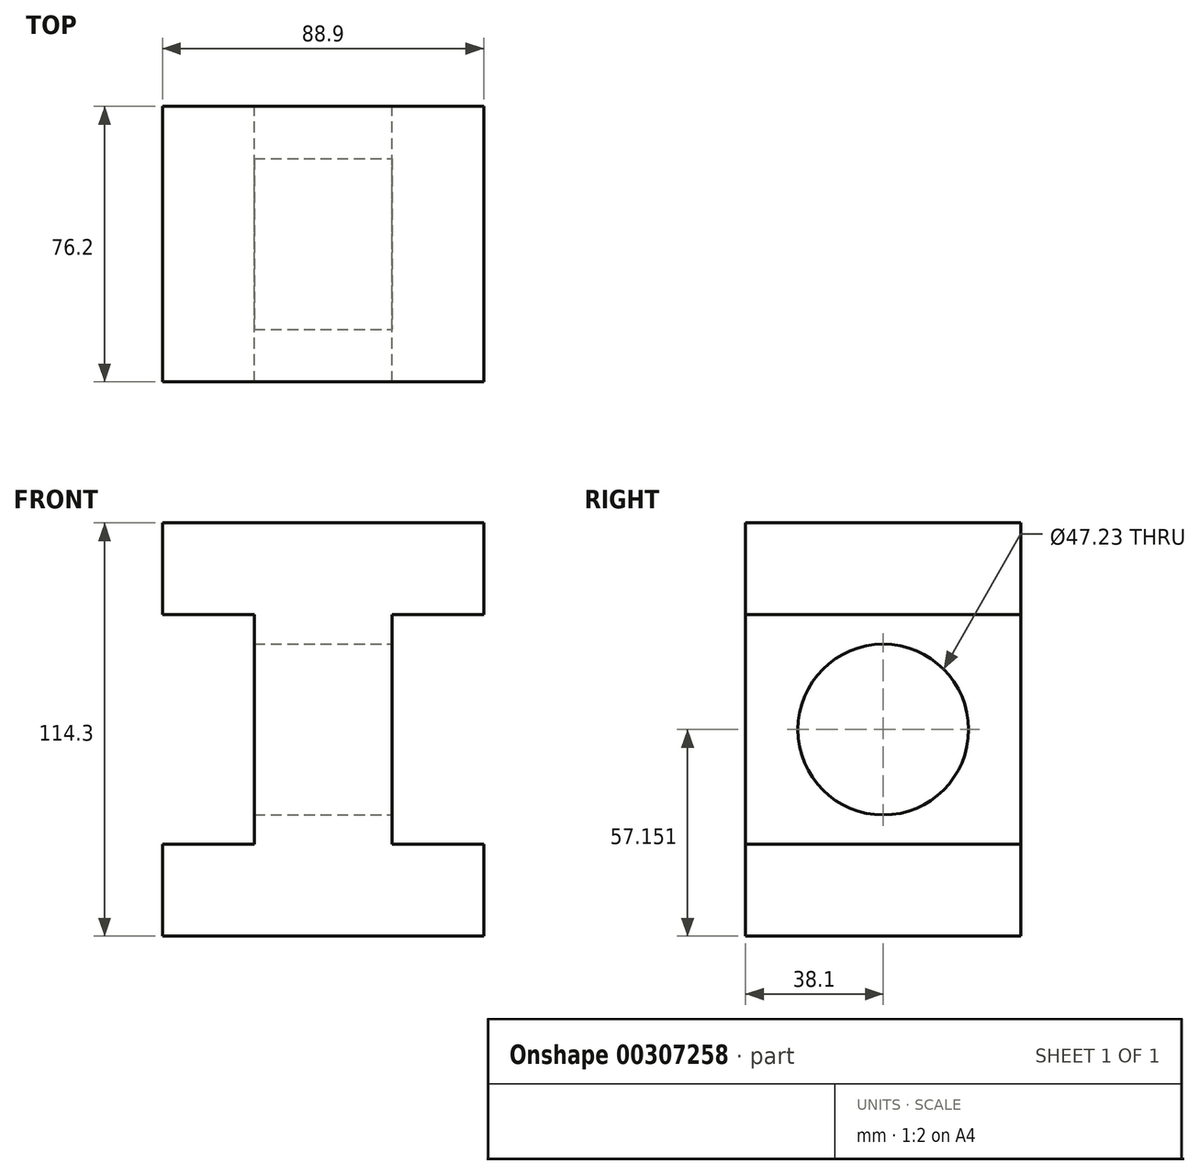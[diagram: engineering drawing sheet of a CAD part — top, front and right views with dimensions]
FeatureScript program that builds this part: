
annotation { "Feature Type Name" : "Feature", "Feature Type Description" : "" }
export const myFeature = defineFeature(function(context is Context, id is Id, definition is map)
    precondition{}
    {
        {
            var Q0;
            Q0=qCreatedBy(makeId("Front.planeOp"),FACE);
            var sketch = newSketch(context, id + "F0", { "sketchPlane" : qUnion([Q0])});
            skLineSegment(sketch, "E0", {"start": v(-48.35, -53.95) * mm, "end": v(40.55, -53.95) * mm});
            skLineSegment(sketch, "E1", {"start": v(40.55, -53.95) * mm, "end": v(40.55, -28.55) * mm});
            skLineSegment(sketch, "E2", {"start": v(40.55, -28.55) * mm, "end": v(15.15, -28.55) * mm});
            skLineSegment(sketch, "E3", {"start": v(15.15, -28.55) * mm, "end": v(15.15, 34.95) * mm});
            skLineSegment(sketch, "E4", {"start": v(15.15, 34.95) * mm, "end": v(40.55, 34.95) * mm});
            skLineSegment(sketch, "E5", {"start": v(40.55, 34.95) * mm, "end": v(40.55, 60.35) * mm});
            skLineSegment(sketch, "E6", {"start": v(40.55, 60.35) * mm, "end": v(-48.35, 60.35) * mm});
            skLineSegment(sketch, "E7", {"start": v(-48.35, 60.35) * mm, "end": v(-48.35, 34.95) * mm});
            skLineSegment(sketch, "E8", {"start": v(-48.35, 34.95) * mm, "end": v(-22.95, 34.95) * mm});
            skLineSegment(sketch, "E9", {"start": v(-22.95, 34.95) * mm, "end": v(-22.95, -28.55) * mm});
            skLineSegment(sketch, "E10", {"start": v(-22.95, -28.55) * mm, "end": v(-48.35, -28.55) * mm});
            skLineSegment(sketch, "E11", {"start": v(-48.35, -28.55) * mm, "end": v(-48.35, -53.95) * mm});
            skSolve(sketch);
        }
        {
            var Q0;
            Q0=makeQuery(id+"F0.imprint","IMPRINT",FACE,{"disambiguationData":[TD([[makeQuery(id+"F0.imprint","IMPRINT",EDGE,{"derivedFrom":sQuery(id+"F0.wireOp",EDGE,"E0")}),1.0]])]});
            extrude(context, id + "F1", {"entities" : qUnion([Q0]), "depth" : 76.2 * mm});
        }
        {
            var Q0;
            Q0=makeQuery(id+"F1.opExtrude","SWEPT_FACE",FACE,{"disambiguationData":[OSD([sQuery(id+"F0.wireOp",EDGE,"E3")])]});
            var sketch = newSketch(context, id + "F2", { "sketchPlane" : qUnion([Q0])});
            skCircle(sketch, "E12", {"center": v(-38.1, 3.2) * mm, "radius": 23.62 * mm});
            skPoint(sketch, "E12.centerSnap0", {"position": v(-38.1, 34.95) * mm});
            skPoint(sketch, "E12.centerSnap1", {"position": v(-76.2, 3.2) * mm});
            skSolve(sketch);
        }
        {
            var Q0;
            Q0=makeQuery(id+"F2.imprint","IMPRINT",FACE,{"disambiguationData":[TD([[makeQuery(id+"F2.imprint","IMPRINT",EDGE,{"derivedFrom":sQuery(id+"F2.wireOp",EDGE,"E12")}),1.0]])]});
            extrude(context, id + "F3", {"entities" : qUnion([Q0]), "operationType" : NewBodyOperationType.REMOVE, "endBound" : BoundingType.THROUGH_ALL, "oppositeDirection" : true, "depth" : 25.4 * mm});
        }
    });
